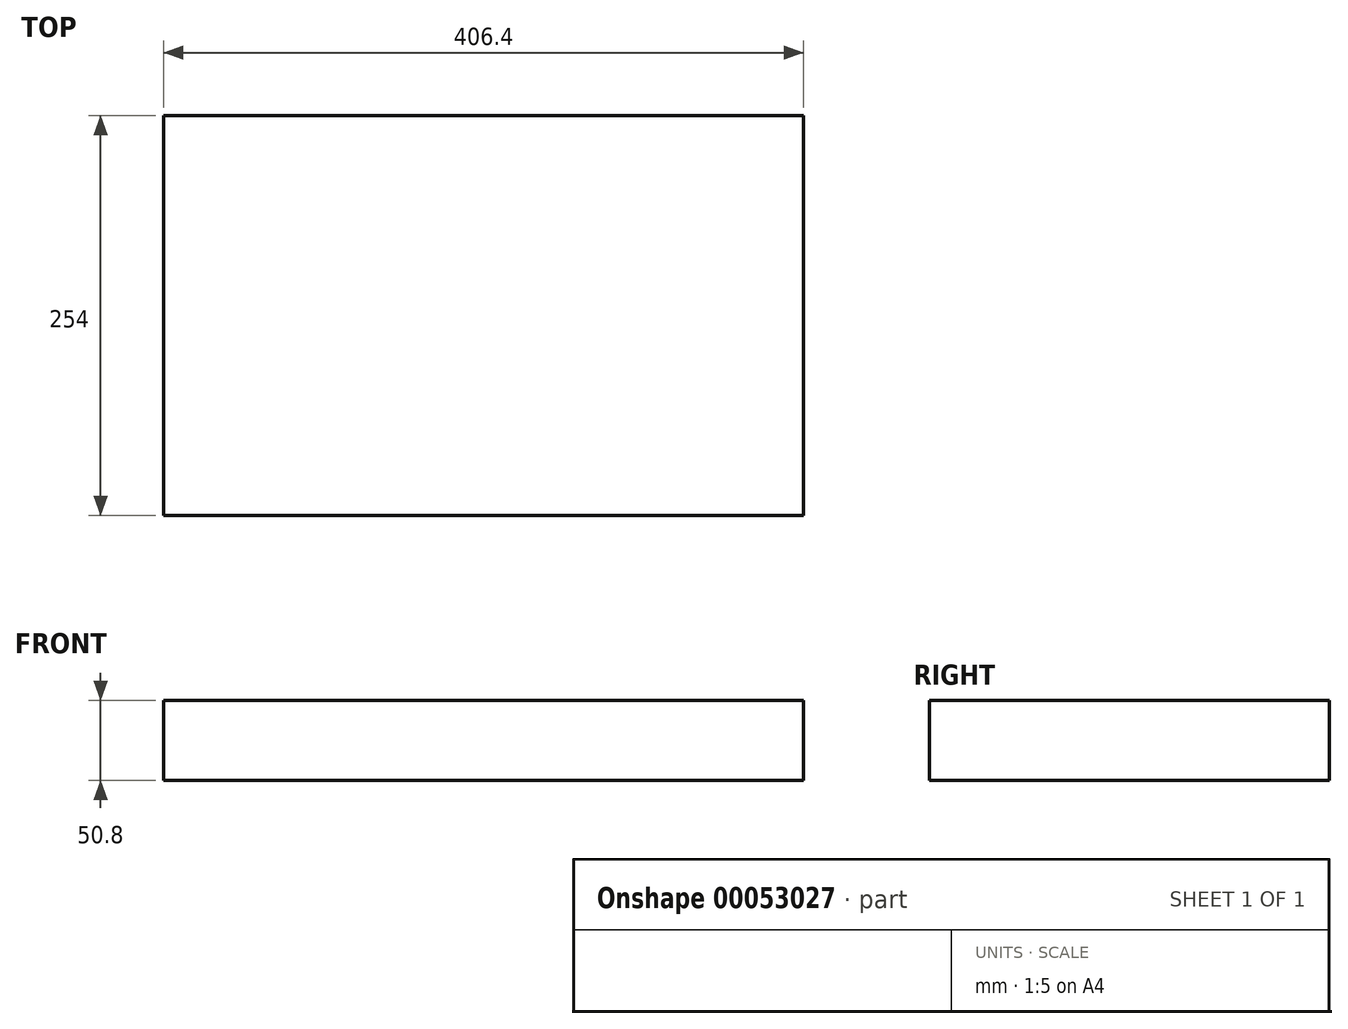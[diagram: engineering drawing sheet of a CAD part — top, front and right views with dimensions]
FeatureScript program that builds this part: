
annotation { "Feature Type Name" : "Feature", "Feature Type Description" : "" }
export const myFeature = defineFeature(function(context is Context, id is Id, definition is map)
    precondition{}
    {
        {
            var Q0;
            Q0=qCreatedBy(makeId("Top.planeOp"),FACE);
            var sketch = newSketch(context, id + "F0", { "sketchPlane" : qUnion([Q0])});
            skLineSegment(sketch, "E0.bottom", {"start": v(0, 0) * mm, "end": v(406.4, 0) * mm});
            skLineSegment(sketch, "E0.top", {"start": v(0, -254) * mm, "end": v(406.4, -254) * mm});
            skLineSegment(sketch, "E0.left", {"start": v(0, 0) * mm, "end": v(0, -254) * mm});
            skLineSegment(sketch, "E0.right", {"start": v(406.4, 0) * mm, "end": v(406.4, -254) * mm});
            skSolve(sketch);
        }
        {
            var Q0;
            Q0 = qSketchRegion(id + "F0", true);
            extrude(context, id + "F1", {"entities" : qUnion([Q0]), "depth" : 50.8 * mm});
        }
    });
